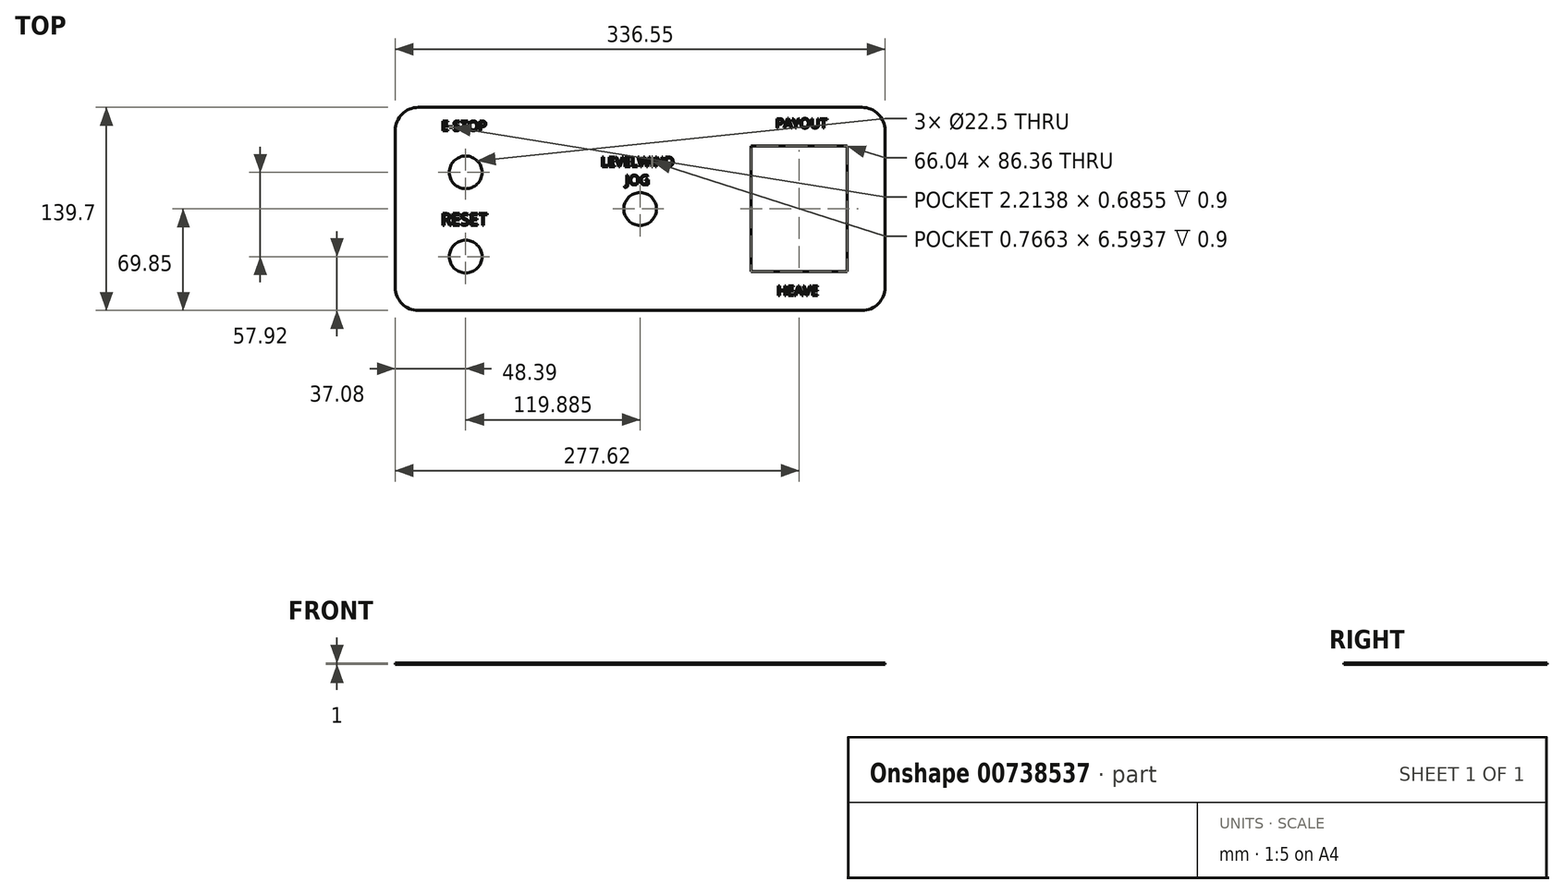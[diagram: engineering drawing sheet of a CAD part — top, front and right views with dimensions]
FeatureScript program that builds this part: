
annotation { "Feature Type Name" : "Feature", "Feature Type Description" : "" }
export const myFeature = defineFeature(function(context is Context, id is Id, definition is map)
    precondition{}
    {
        {
            var Q0;
            Q0=qCreatedBy(makeId("Top.planeOp"),FACE);
            var sketch = newSketch(context, id + "F0", { "sketchPlane" : qUnion([Q0])});
            skLineSegment(sketch, "E0.bottom", {"start": v(0, 0) * mm, "end": v(336.55, 0) * mm});
            skLineSegment(sketch, "E0.top", {"start": v(0, 139.7) * mm, "end": v(336.55, 139.7) * mm});
            skLineSegment(sketch, "E0.left", {"start": v(0, 0) * mm, "end": v(0, 139.7) * mm});
            skLineSegment(sketch, "E0.right", {"start": v(336.55, 0) * mm, "end": v(336.55, 139.7) * mm});
            skLineSegment(sketch, "E1.bottom", {"start": v(244.6, 113.03) * mm, "end": v(310.64, 113.03) * mm});
            skLineSegment(sketch, "E1.top", {"start": v(244.6, 26.67) * mm, "end": v(310.64, 26.67) * mm});
            skLineSegment(sketch, "E1.left", {"start": v(244.6, 113.03) * mm, "end": v(244.6, 26.67) * mm});
            skLineSegment(sketch, "E1.right", {"start": v(310.64, 113.03) * mm, "end": v(310.64, 26.67) * mm});
            skCircle(sketch, "E2", {"center": v(168.28, 69.85) * mm, "radius": 11.25 * mm});
            skPoint(sketch, "E2.centerSnap0", {"position": v(168.28, 0) * mm});
            skCircle(sketch, "E3", {"center": v(48.4, 37.08) * mm, "radius": 11.25 * mm});
            skCircle(sketch, "E4", {"center": v(48.39, 95) * mm, "radius": 11.25 * mm});
            skSolve(sketch);
        }
        {
            var Q0;
            Q0 = qSketchRegion(id + "F0", true);
            extrude(context, id + "F1", {"entities" : qUnion([Q0]), "depth" : 1 * mm, "offsetDistance" : 25 * mm});
        }
        {
            var Q0;
            Q0=makeQuery(id+"F1.opExtrude","SWEPT_EDGE",EDGE,{"disambiguationData":[OSD([sQuery(id+"F0.wireOp",EDGE,"E0.bottom"),sQuery(id+"F0.wireOp",EDGE,"E0.left")])]});
            var Q1;
            Q1=makeQuery(id+"F1.opExtrude","SWEPT_EDGE",EDGE,{"disambiguationData":[OSD([sQuery(id+"F0.wireOp",EDGE,"E0.bottom"),sQuery(id+"F0.wireOp",EDGE,"E0.right")])]});
            var Q2;
            Q2=makeQuery(id+"F1.opExtrude","SWEPT_EDGE",EDGE,{"disambiguationData":[OSD([sQuery(id+"F0.wireOp",EDGE,"E0.top"),sQuery(id+"F0.wireOp",EDGE,"E0.right")])]});
            var Q3;
            Q3=makeQuery(id+"F1.opExtrude","SWEPT_EDGE",EDGE,{"disambiguationData":[OSD([sQuery(id+"F0.wireOp",EDGE,"E0.top"),sQuery(id+"F0.wireOp",EDGE,"E0.left")])]});
            fillet(context, id + "F2", {"entities" : qUnion([Q0, Q1, Q2, Q3]), "radius" : 15.88 * mm, "tangentPropagation" : true, "allowEdgeOverflow" : false});
        }
        {
            var Q0;
            Q0=makeQuery(id+"F1.opExtrude","CAP_FACE",FACE,{"disambiguationData":[OSD([sQuery(id+"F0.wireOp",EDGE,"E0.bottom"),sQuery(id+"F0.wireOp",EDGE,"E0.top"),sQuery(id+"F0.wireOp",EDGE,"E0.left"),sQuery(id+"F0.wireOp",EDGE,"E0.right"),sQuery(id+"F0.wireOp",EDGE,"E1.bottom"),sQuery(id+"F0.wireOp",EDGE,"E1.top"),sQuery(id+"F0.wireOp",EDGE,"E1.left"),sQuery(id+"F0.wireOp",EDGE,"E1.right"),sQuery(id+"F0.wireOp",EDGE,"E2"),sQuery(id+"F0.wireOp",EDGE,"E3"),sQuery(id+"F0.wireOp",EDGE,"E4")])],"isStart":false});
            var sketch = newSketch(context, id + "F3", { "sketchPlane" : qUnion([Q0])});
            skText(sketch, "E5", { "text": "E-STOP\n", "fontName": "OpenSans-Regular.ttf"});
            skText(sketch, "E6", { "text": "RESET", "fontName": "OpenSans-Regular.ttf"});
            skText(sketch, "E7", { "text": "LEVELWIND\n       JOG", "fontName": "OpenSans-Regular.ttf"});
            skText(sketch, "E8", { "text": "PAYOUT", "fontName": "OpenSans-Regular.ttf"});
            skText(sketch, "E9", { "text": "HEAVE", "fontName": "OpenSans-Regular.ttf"});
            const initialGuessF3  = {"E5": [0.03172, 0.12374, 1, 0, 0.00665], "E6": [0.03172, 0.0587, 1, 0, 0.00806], "E7": [0.14138, 0.09901, 1, 0, 0.00665], "E8": [0.26133, 0.12547, 1, 0, 0.00665], "E9": [0.2624, 0.01035, 1, 0, 0.00665]};
            skSetInitialGuess(sketch, initialGuessF3);
            skSolve(sketch);
        }
        {
            var Q0;
            Q0 = qSketchRegion(id + "F3", true);
            extrude(context, id + "F4", {"entities" : qUnion([Q0]), "operationType" : NewBodyOperationType.REMOVE, "oppositeDirection" : true, "depth" : .9 * mm, "offsetDistance" : 25 * mm});
        }
    });
